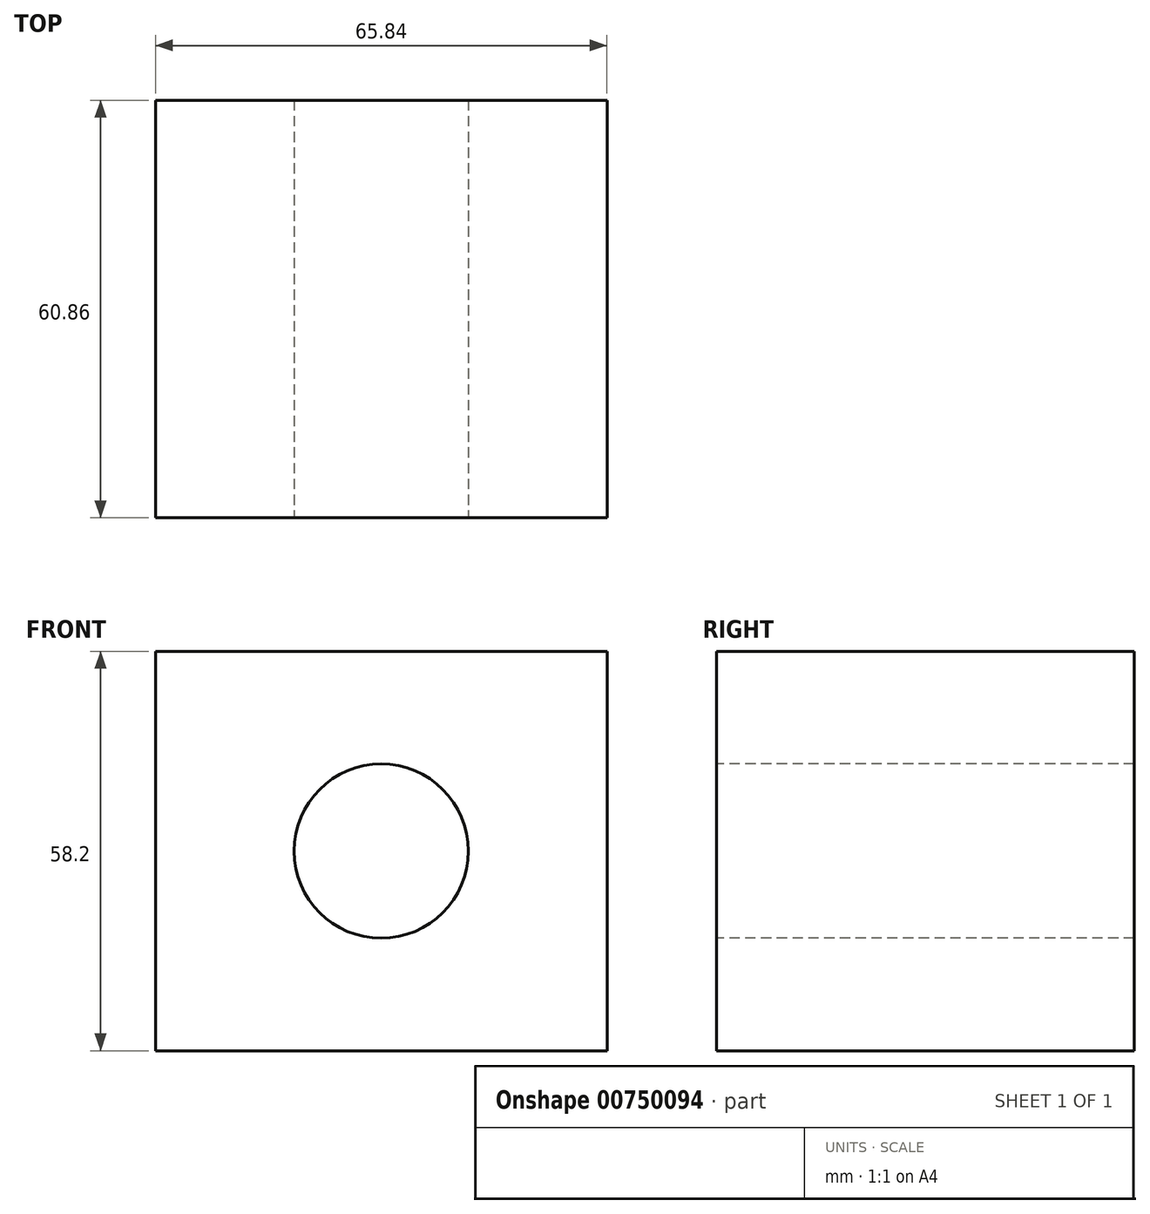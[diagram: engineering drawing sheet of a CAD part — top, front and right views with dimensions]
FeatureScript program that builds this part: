
annotation { "Feature Type Name" : "Feature", "Feature Type Description" : "" }
export const myFeature = defineFeature(function(context is Context, id is Id, definition is map)
    precondition{}
    {
        {
            var Q0;
            Q0=qCreatedBy(makeId("Front.planeOp"),FACE);
            var sketch = newSketch(context, id + "F0", { "sketchPlane" : qUnion([Q0])});
            skLineSegment(sketch, "E0.bottom", {"start": v(32.92, -29.1) * mm, "end": v(-32.92, -29.1) * mm});
            skLineSegment(sketch, "E0.top", {"start": v(32.92, 29.1) * mm, "end": v(-32.92, 29.1) * mm});
            skLineSegment(sketch, "E0.left", {"start": v(32.92, -29.1) * mm, "end": v(32.92, 29.1) * mm});
            skLineSegment(sketch, "E0.right", {"start": v(-32.92, -29.1) * mm, "end": v(-32.92, 29.1) * mm});
            skPoint(sketch, "E0.middle", {"position": v(0, 0) * mm});
            skSolve(sketch);
        }
        {
            var Q0;
            Q0=makeQuery(id+"F0.imprint","IMPRINT",FACE,{"disambiguationData":[TD([[makeQuery(id+"F0.imprint","IMPRINT",EDGE,{"derivedFrom":sQuery(id+"F0.wireOp",EDGE,"E0.bottom")}),-1.0]])]});
            extrude(context, id + "F1", {"entities" : qUnion([Q0]), "depth" : 60.86 * mm, "offsetDistance" : 25.4 * mm});
        }
        {
            var Q0;
            Q0=makeQuery(id+"F1.opExtrude","CAP_FACE",FACE,{"disambiguationData":[OSD([sQuery(id+"F0.wireOp",EDGE,"E0.bottom"),sQuery(id+"F0.wireOp",EDGE,"E0.top"),sQuery(id+"F0.wireOp",EDGE,"E0.left"),sQuery(id+"F0.wireOp",EDGE,"E0.right")])],"isStart":false});
            var sketch = newSketch(context, id + "F2", { "sketchPlane" : qUnion([Q0])});
            skCircle(sketch, "E1", {"center": v(0, 0) * mm, "radius": 13.44 * mm});
            skSolve(sketch);
        }
        {
            var Q0;
            Q0 = qSketchRegion(id + "F2", true);
            var sketch = newSketch(context, id + "F3", { "sketchPlane" : qUnion([Q0])});
            skPoint(sketch, "E2", {"position": v(0, 0) * mm});
            skSolve(sketch);
        }
        {
            var Q0;
            Q0=sQuery(id+"F3.wireOp",VERTEX,"E2");
            var Q1;
            Q1=makeQuery(id+"F1.opExtrude","SWEPT_BODY",BODY,{"disambiguationData":[OSD([sQuery(id+"F0.wireOp",EDGE,"E0.bottom"),sQuery(id+"F0.wireOp",EDGE,"E0.top"),sQuery(id+"F0.wireOp",EDGE,"E0.left"),sQuery(id+"F0.wireOp",EDGE,"E0.right")])]});
            hole(context, id + "F4", {"style" : HoleStyle.SIMPLE, "endStyle" : HoleEndStyle.THROUGH, "holeDiameter" : 25.4 * mm, "majorDiameter" : 6.35 * mm, "isTappedThrough" : true, "tappedDepth" : 12.7 * mm, "tapClearance" : 3, "locations" : qUnion([Q0]), "scope" : qUnion([Q1])});
        }
    });
